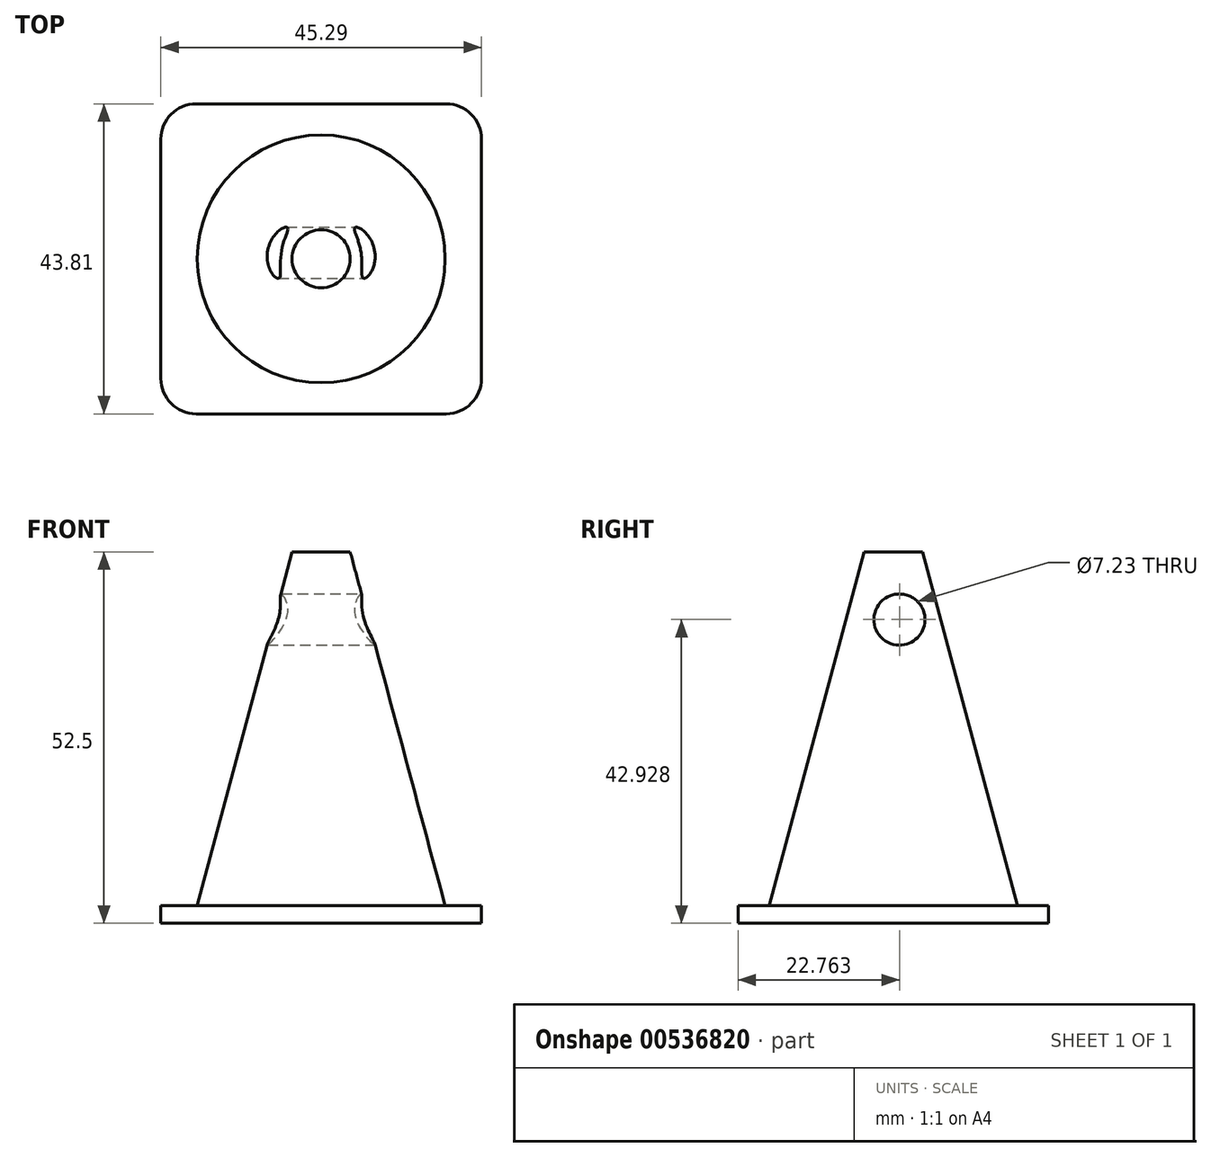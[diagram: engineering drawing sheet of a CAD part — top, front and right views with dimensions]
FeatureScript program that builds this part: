
annotation { "Feature Type Name" : "Feature", "Feature Type Description" : "" }
export const myFeature = defineFeature(function(context is Context, id is Id, definition is map)
    precondition{}
    {
        {
            var Q0;
            Q0=qCreatedBy(makeId("Top.planeOp"),FACE);
            var sketch = newSketch(context, id + "F0", { "sketchPlane" : qUnion([Q0])});
            skArc(sketch, "E0", {"start": v(-35.3, 38.8) * mm, "mid": v(-38.83, 37.34) * mm, "end": v(-40.3, 33.8) * mm});
            skArc(sketch, "E1", {"start": v(-40.3, 0) * mm, "mid": v(-38.83, -3.54) * mm, "end": v(-35.3, -5) * mm});
            skArc(sketch, "E2", {"start": v(0, -5) * mm, "mid": v(3.54, -3.54) * mm, "end": v(5, 0) * mm});
            skArc(sketch, "E3", {"start": v(5, 33.8) * mm, "mid": v(3.54, 37.34) * mm, "end": v(0, 38.8) * mm});
            skLineSegment(sketch, "E4", {"start": v(-40.3, 33.8) * mm, "end": v(-40.3, 0) * mm});
            skLineSegment(sketch, "E5", {"start": v(-35.3, -5) * mm, "end": v(0, -5) * mm});
            skLineSegment(sketch, "E6", {"start": v(5, 0) * mm, "end": v(5, 33.8) * mm});
            skLineSegment(sketch, "E7", {"start": v(-35.3, 38.8) * mm, "end": v(0, 38.8) * mm});
            skCircle(sketch, "E8", {"center": v(-17.65, 16.9) * mm, "radius": 17.5 * mm});
            skSolve(sketch);
        }
        {
            var Q0;
            Q0=makeQuery(id+"F0.imprint","IMPRINT",FACE,{"disambiguationData":[TD([[makeQuery(id+"F0.imprint","IMPRINT",EDGE,{"derivedFrom":sQuery(id+"F0.wireOp",EDGE,"E0")}),1.0]])]});
            var Q1;
            Q1=makeQuery(id+"F0.imprint","IMPRINT",FACE,{"disambiguationData":[TD([[makeQuery(id+"F0.imprint","IMPRINT",EDGE,{"derivedFrom":sQuery(id+"F0.wireOp",EDGE,"E8")}),1.0]])]});
            extrude(context, id + "F1", {"entities" : qUnion([Q0, Q1]), "depth" : 2.5 * mm, "offsetDistance" : 25 * mm});
        }
        {
            var Q0;
            Q0=makeQuery(id+"F1.opExtrude","CAP_FACE",FACE,{"disambiguationData":[OSD([sQuery(id+"F0.wireOp",EDGE,"E0"),sQuery(id+"F0.wireOp",EDGE,"E1"),sQuery(id+"F0.wireOp",EDGE,"E2"),sQuery(id+"F0.wireOp",EDGE,"E3"),sQuery(id+"F0.wireOp",EDGE,"E4"),sQuery(id+"F0.wireOp",EDGE,"E5"),sQuery(id+"F0.wireOp",EDGE,"E6"),sQuery(id+"F0.wireOp",EDGE,"E7")])],"isStart":false});
            var sketch = newSketch(context, id + "F2", { "sketchPlane" : qUnion([Q0])});
            skCircle(sketch, "E9", {"center": v(-17.65, 16.9) * mm, "radius": 17.5 * mm});
            skPoint(sketch, "E10.orphan", {"position": v(-40.3, 16.9) * mm});
            skPoint(sketch, "E11.orphan", {"position": v(-17.65, -5) * mm});
            skPoint(sketch, "E12.start.orphan", {"position": v(5, 16.9) * mm});
            skPoint(sketch, "E13.start.orphan", {"position": v(-17.65, 38.8) * mm});
            skSolve(sketch);
        }
        {
            var Q0;
            Q0=makeQuery(id+"F2.imprint","IMPRINT",FACE,{"disambiguationData":[TD([[makeQuery(id+"F2.imprint","IMPRINT",EDGE,{"derivedFrom":sQuery(id+"F2.wireOp",EDGE,"E9")}),1.0]])]});
            extrude(context, id + "F3", {"entities" : qUnion([Q0]), "operationType" : NewBodyOperationType.ADD, "depth" : 50 * mm, "offsetDistance" : 25 * mm, "hasDraft" : true, "draftAngle" : 15 * degree, "draftPullDirection" : true});
        }
        {
            var Q0;
            Q0=qCreatedBy(makeId("Right.planeOp"),FACE);
            var sketch = newSketch(context, id + "F4", { "sketchPlane" : qUnion([Q0])});
            skCircle(sketch, "E14", {"center": v(17.76, 42.93) * mm, "radius": 3.61 * mm});
            skSolve(sketch);
        }
        {
            var Q0;
            Q0=qSketchRegion(id+"F4",true);
            extrude(context, id + "F5", {"entities" : qUnion([Q0]), "operationType" : NewBodyOperationType.REMOVE, "oppositeDirection" : true, "depth" : 60 * mm, "offsetDistance" : 25 * mm});
        }
    });
